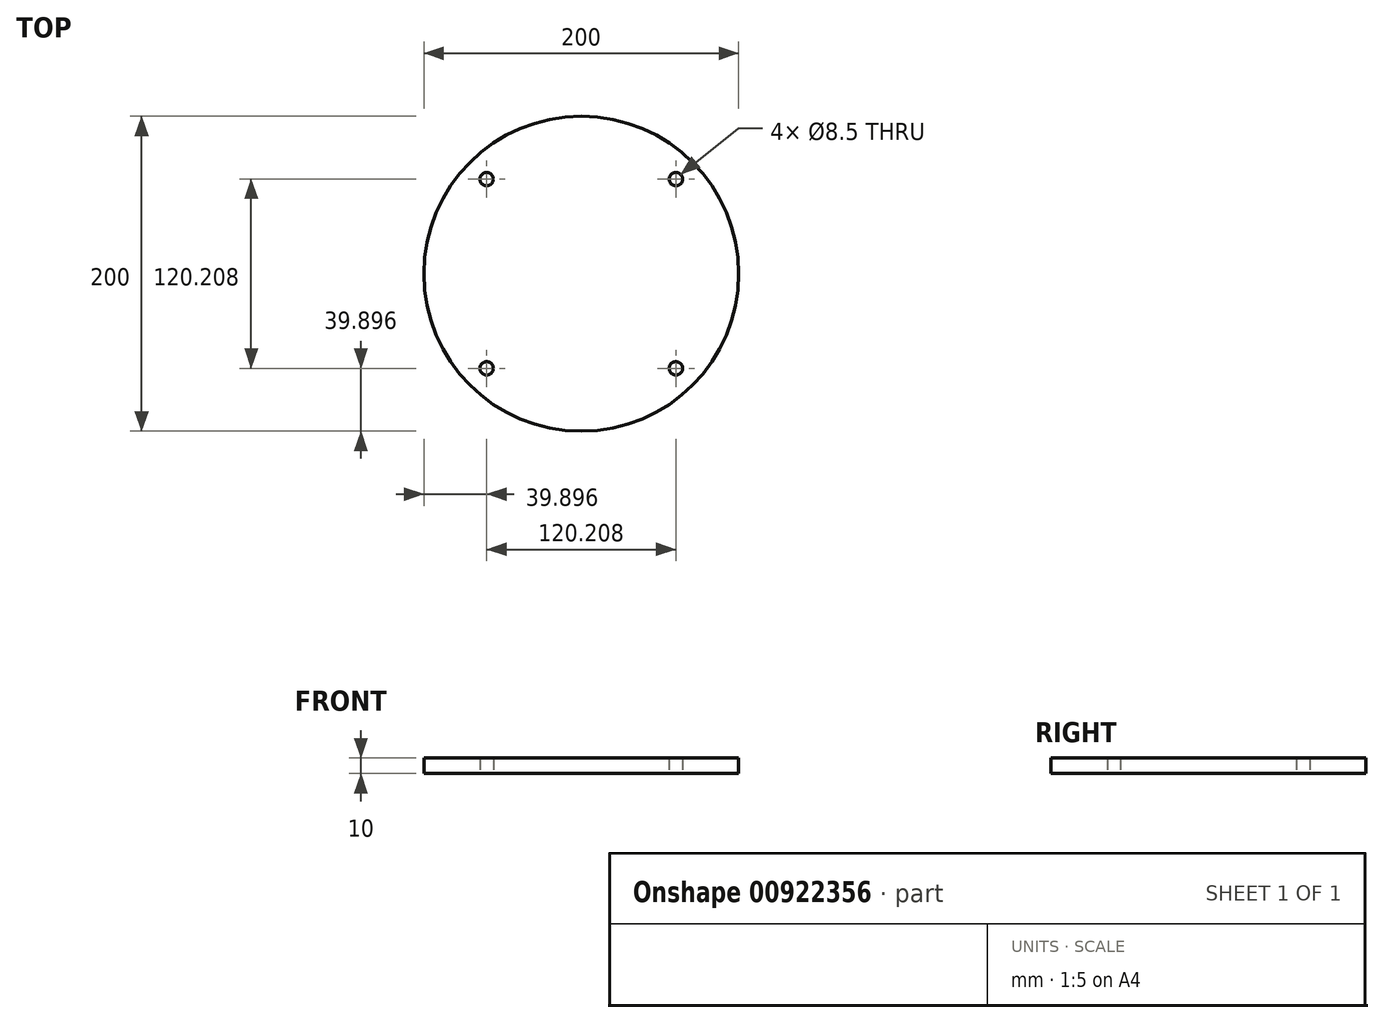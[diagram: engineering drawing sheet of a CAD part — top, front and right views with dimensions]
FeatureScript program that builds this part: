
annotation { "Feature Type Name" : "Feature", "Feature Type Description" : "" }
export const myFeature = defineFeature(function(context is Context, id is Id, definition is map)
    precondition{}
    {
        {
            var Q0;
            Q0=qCreatedBy(makeId("Top.planeOp"),FACE);
            var sketch = newSketch(context, id + "F0", { "sketchPlane" : qUnion([Q0])});
            skCircle(sketch, "E0", {"center": v(0, 0) * mm, "radius": 85 * mm});
            skLineSegment(sketch, "E1", {"start": v(0, 0) * mm, "end": v(-60.1, 60.1) * mm});
            skLineSegment(sketch, "E2", {"start": v(60.1, 60.1) * mm, "end": v(0, 0) * mm});
            skLineSegment(sketch, "E3", {"start": v(0, 0) * mm, "end": v(-60.1, -60.1) * mm});
            skLineSegment(sketch, "E4", {"start": v(60.1, -60.1) * mm, "end": v(0, 0) * mm});
            skPoint(sketch, "E5", {"position": v(-60.1, 60.1) * mm});
            skPoint(sketch, "E6", {"position": v(60.1, 60.1) * mm});
            skPoint(sketch, "E7", {"position": v(60.1, -60.1) * mm});
            skPoint(sketch, "E8", {"position": v(-60.1, -60.1) * mm});
            skSolve(sketch);
        }
        {
            var Q0;
            Q0=qCreatedBy(makeId("Top.planeOp"),FACE);
            var sketch = newSketch(context, id + "F1", { "sketchPlane" : qUnion([Q0])});
            skCircle(sketch, "E9", {"center": v(0, 0) * mm, "radius": 100 * mm});
            skSolve(sketch);
        }
        {
            var Q0;
            Q0=makeQuery(id+"F1.imprint","IMPRINT",FACE,{"disambiguationData":[TD([[makeQuery(id+"F1.imprint","IMPRINT",EDGE,{"derivedFrom":sQuery(id+"F1.wireOp",EDGE,"E9")}),1.0]])]});
            extrude(context, id + "F2", {"entities" : qUnion([Q0]), "depth" : 10 * mm, "offsetDistance" : 25 * mm});
        }
        {
            var Q0;
            Q0=sQuery(id+"F0.wireOp",VERTEX,"E5");
            var Q1;
            Q1=sQuery(id+"F0.wireOp",VERTEX,"E6");
            var Q2;
            Q2=sQuery(id+"F0.wireOp",VERTEX,"E7");
            var Q3;
            Q3=sQuery(id+"F0.wireOp",VERTEX,"E8");
            var Q4;
            Q4=makeQuery(id+"F2.opExtrude","SWEPT_BODY",BODY,{"disambiguationData":[OSD([sQuery(id+"F1.wireOp",EDGE,"E9")])]});
            hole(context, id + "F3", {"style" : HoleStyle.SIMPLE, "endStyle" : HoleEndStyle.THROUGH, "oppositeDirection" : true, "holeDiameter" : 8.5 * mm, "majorDiameter" : 5 * mm, "isTappedThrough" : true, "tappedDepth" : 12 * mm, "tapClearance" : 3, "locations" : qUnion([Q0, Q1, Q2, Q3]), "scope" : qUnion([Q4])});
        }
    });
